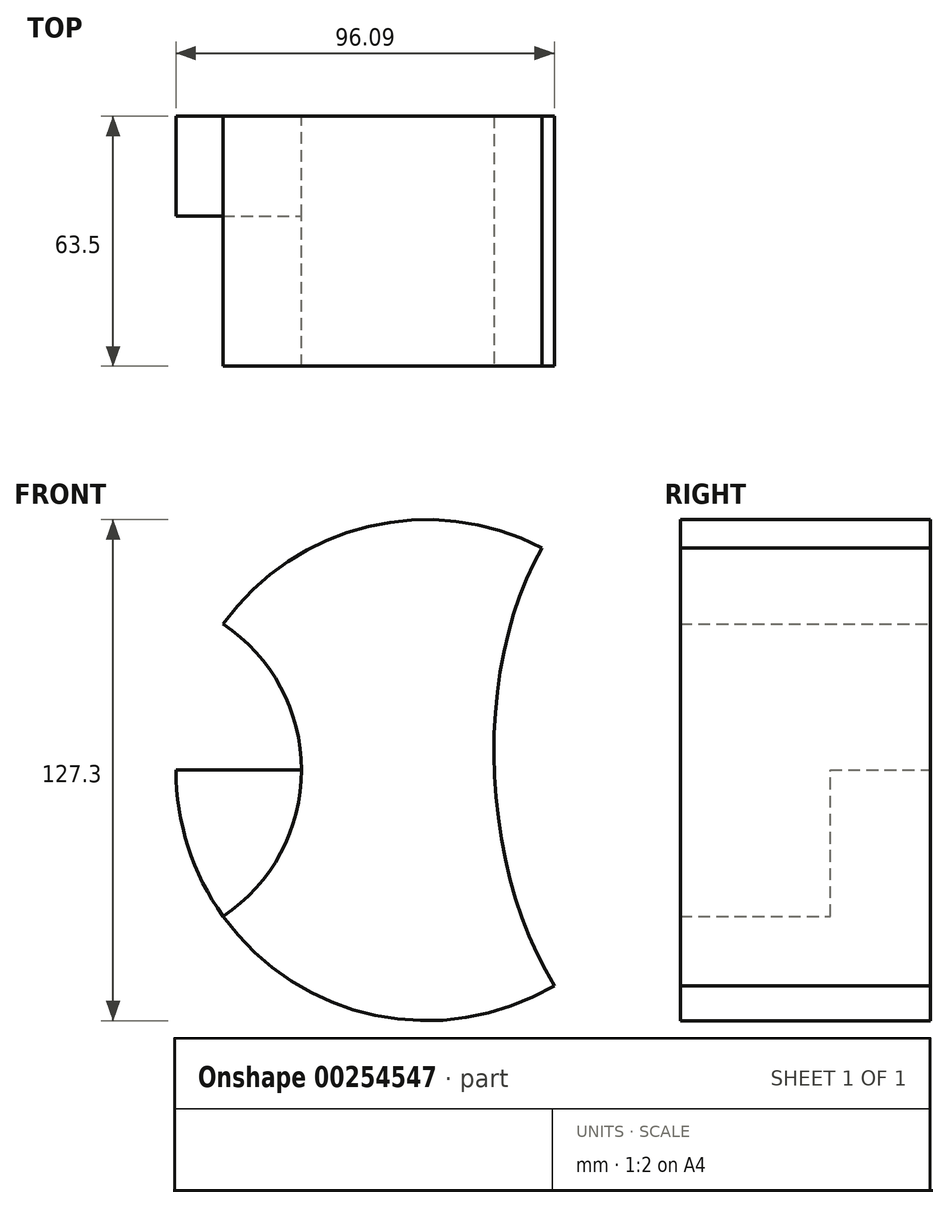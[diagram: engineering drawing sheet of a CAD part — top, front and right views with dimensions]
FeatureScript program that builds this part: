
annotation { "Feature Type Name" : "Feature", "Feature Type Description" : "" }
export const myFeature = defineFeature(function(context is Context, id is Id, definition is map)
    precondition{}
    {
        {
            var Q0;
            Q0=qCreatedBy(makeId("Front.planeOp"),FACE);
            var sketch = newSketch(context, id + "F0", { "sketchPlane" : qUnion([Q0])});
            skCircle(sketch, "E0", {"center": v(-76.2, 0) * mm, "radius": 44.45 * mm});
            skLineSegment(sketch, "E1", {"start": v(-76.2, 0) * mm, "end": v(0, 0) * mm});
            skLineSegment(sketch, "E2", {"start": v(-31.75, 0) * mm, "end": v(-63.5, 0) * mm});
            skCircle(sketch, "E3", {"center": v(0, 0) * mm, "radius": 63.65 * mm});
            skLineSegment(sketch, "E4", {"start": v(63.65, 0) * mm, "end": v(63.65, 35.58) * mm});
            skEllipse(sketch, "E5", {"center": v(63.65, 0) * mm, "majorRadius": 78.48 * mm, "minorRadius": 46.4 * mm, "majorAxis": v(0.06, -1)});
            skSolve(sketch);
        }
        {
            var Q0;
            {var subQ1=sQuery(id+"F0.wireOp",EDGE,"E0");var subQ5=makeQuery(id+"F0.imprint","INTERSECT",VERTEX,{"derivedFrom":[subQ1,sQuery(id+"F0.wireOp",EDGE,"E2")]});Q0=makeQuery(id+"F0.imprint","IMPRINT",FACE,{"disambiguationData":[TD([[makeQuery(id+"F0.imprint","IMPRINT",EDGE,{"disambiguationData":[TD([[subQ5,-1.0]])],"derivedFrom":subQ1}),-1.0]])]});}
            var Q1;
            {var subQ0=sQuery(id+"F0.wireOp",EDGE,"E2");Q1=makeQuery(id+"F0.imprint","IMPRINT",FACE,{"disambiguationData":[TD([[makeQuery(id+"F0.imprint","IMPRINT",EDGE,{"derivedFrom":subQ0}),-1.0]])]});}
            var Q2;
            {var subQ0=sQuery(id+"F0.wireOp",EDGE,"E2");Q2=makeQuery(id+"F0.imprint","IMPRINT",FACE,{"disambiguationData":[TD([[makeQuery(id+"F0.imprint","IMPRINT",EDGE,{"derivedFrom":subQ0}),1.0]])]});}
            extrude(context, id + "F1", {"entities" : qUnion([Q0, Q1, Q2]), "depth" : 63.5 * mm});
        }
        {
            var Q0;
            {var subQ0=sQuery(id+"F0.wireOp",EDGE,"E3");var subQ1=sQuery(id+"F0.wireOp",EDGE,"E0");var subQ2=makeQuery(id+"F0.imprint","INTERSECT",VERTEX,{"disambiguationData":[OD(0.0)],"derivedFrom":[subQ1,subQ0]});Q0=makeQuery(id+"F0.imprint","IMPRINT",FACE,{"disambiguationData":[TD([[makeQuery(id+"F0.imprint","IMPRINT",EDGE,{"disambiguationData":[TD([[subQ2,-1.0]])],"derivedFrom":subQ1}),1.0]])]});}
            extrude(context, id + "F2", {"entities" : qUnion([Q0]), "operationType" : NewBodyOperationType.ADD, "depth" : 25.4 * mm});
        }
    });
